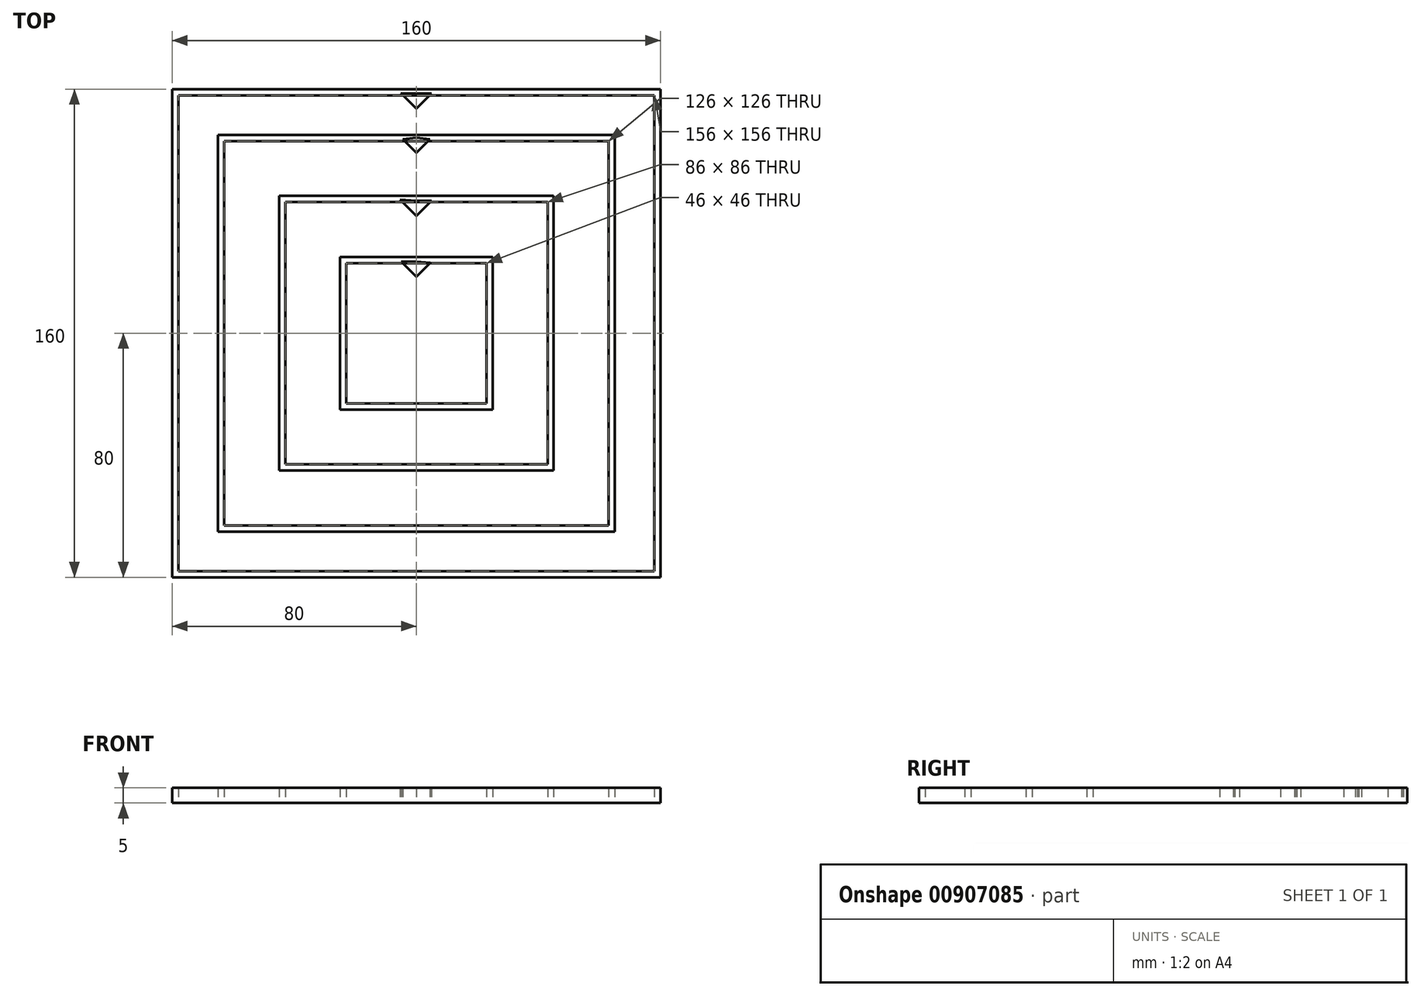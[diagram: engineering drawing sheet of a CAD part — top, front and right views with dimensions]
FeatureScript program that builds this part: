
annotation { "Feature Type Name" : "Feature", "Feature Type Description" : "" }
export const myFeature = defineFeature(function(context is Context, id is Id, definition is map)
    precondition{}
    {
        {
            var Q0;
            Q0=qCreatedBy(makeId("Top.planeOp"),FACE);
            var sketch = newSketch(context, id + "F0", { "sketchPlane" : qUnion([Q0])});
            skLineSegment(sketch, "E0.bottom", {"start": v(-80, 80) * mm, "end": v(80, 80) * mm});
            skLineSegment(sketch, "E0.top", {"start": v(-80, -80) * mm, "end": v(80, -80) * mm});
            skLineSegment(sketch, "E0.left", {"start": v(-80, 80) * mm, "end": v(-80, -80) * mm});
            skLineSegment(sketch, "E0.right", {"start": v(80, 80) * mm, "end": v(80, -80) * mm});
            skPoint(sketch, "E0.middle", {"position": v(0, 0) * mm});
            skLineSegment(sketch, "E1.bottom", {"start": v(-78, 78) * mm, "end": v(78, 78) * mm});
            skLineSegment(sketch, "E1.top", {"start": v(-78, -78) * mm, "end": v(78, -78) * mm});
            skLineSegment(sketch, "E1.left", {"start": v(-78, 78) * mm, "end": v(-78, -78) * mm});
            skLineSegment(sketch, "E1.right", {"start": v(78, 78) * mm, "end": v(78, -78) * mm});
            skLineSegment(sketch, "E2.bottom", {"start": v(-45, 45) * mm, "end": v(45, 45) * mm});
            skLineSegment(sketch, "E2.top", {"start": v(-45, -45) * mm, "end": v(45, -45) * mm});
            skLineSegment(sketch, "E2.left", {"start": v(-45, 45) * mm, "end": v(-45, -45) * mm});
            skLineSegment(sketch, "E2.right", {"start": v(45, 45) * mm, "end": v(45, -45) * mm});
            skLineSegment(sketch, "E3.bottom", {"start": v(-43, 43) * mm, "end": v(43, 43) * mm});
            skLineSegment(sketch, "E3.top", {"start": v(-43, -43) * mm, "end": v(43, -43) * mm});
            skLineSegment(sketch, "E3.left", {"start": v(-43, 43) * mm, "end": v(-43, -43) * mm});
            skLineSegment(sketch, "E3.right", {"start": v(43, 43) * mm, "end": v(43, -43) * mm});
            skLineSegment(sketch, "E4.bottom", {"start": v(-25, 25) * mm, "end": v(25, 25) * mm});
            skLineSegment(sketch, "E4.top", {"start": v(-25, -25) * mm, "end": v(25, -25) * mm});
            skLineSegment(sketch, "E4.left", {"start": v(-25, 25) * mm, "end": v(-25, -25) * mm});
            skLineSegment(sketch, "E4.right", {"start": v(25, 25) * mm, "end": v(25, -25) * mm});
            skLineSegment(sketch, "E5.bottom", {"start": v(-23, 23) * mm, "end": v(23, 23) * mm});
            skLineSegment(sketch, "E5.top", {"start": v(-23, -23) * mm, "end": v(23, -23) * mm});
            skLineSegment(sketch, "E5.left", {"start": v(-23, 23) * mm, "end": v(-23, -23) * mm});
            skLineSegment(sketch, "E5.right", {"start": v(23, 23) * mm, "end": v(23, -23) * mm});
            skLineSegment(sketch, "E6.bottom", {"start": v(-65, 65) * mm, "end": v(65, 65) * mm});
            skLineSegment(sketch, "E6.top", {"start": v(-65, -65) * mm, "end": v(65, -65) * mm});
            skLineSegment(sketch, "E6.left", {"start": v(-65, 65) * mm, "end": v(-65, -65) * mm});
            skLineSegment(sketch, "E6.right", {"start": v(65, 65) * mm, "end": v(65, -65) * mm});
            skLineSegment(sketch, "E7.bottom", {"start": v(-63, 63) * mm, "end": v(63, 63) * mm});
            skLineSegment(sketch, "E7.top", {"start": v(-63, -63) * mm, "end": v(63, -63) * mm});
            skLineSegment(sketch, "E7.left", {"start": v(-63, 63) * mm, "end": v(-63, -63) * mm});
            skLineSegment(sketch, "E7.right", {"start": v(63, 63) * mm, "end": v(63, -63) * mm});
            skSolve(sketch);
        }
        {
            var Q0;
            Q0=makeQuery(id+"F0.imprint","IMPRINT",FACE,{"disambiguationData":[TD([[makeQuery(id+"F0.imprint","IMPRINT",EDGE,{"derivedFrom":sQuery(id+"F0.wireOp",EDGE,"E0.bottom")}),-1.0]])]});
            var Q1;
            Q1=makeQuery(id+"F0.imprint","IMPRINT",FACE,{"disambiguationData":[TD([[makeQuery(id+"F0.imprint","IMPRINT",EDGE,{"derivedFrom":sQuery(id+"F0.wireOp",EDGE,"E6.bottom")}),-1.0]])]});
            var Q2;
            Q2=makeQuery(id+"F0.imprint","IMPRINT",FACE,{"disambiguationData":[TD([[makeQuery(id+"F0.imprint","IMPRINT",EDGE,{"derivedFrom":sQuery(id+"F0.wireOp",EDGE,"E2.bottom")}),-1.0]])]});
            var Q3;
            Q3=makeQuery(id+"F0.imprint","IMPRINT",FACE,{"disambiguationData":[TD([[makeQuery(id+"F0.imprint","IMPRINT",EDGE,{"derivedFrom":sQuery(id+"F0.wireOp",EDGE,"E4.bottom")}),-1.0]])]});
            extrude(context, id + "F1", {"entities" : qUnion([Q0, Q1, Q2, Q3]), "depth" : 5 * mm, "offsetDistance" : 25 * mm});
        }
        {
            var Q0;
            Q0=qCreatedBy(makeId("Top.planeOp"),FACE);
            var sketch = newSketch(context, id + "F2", { "sketchPlane" : qUnion([Q0])});
            skLineSegment(sketch, "E8", {"start": v(0, 78.6) * mm, "end": v(0, 73.6) * mm});
            skLineSegment(sketch, "E9", {"start": v(0, 73.6) * mm, "end": v(-5.12, 78.73) * mm});
            skLineSegment(sketch, "E10", {"start": v(-5.12, 78.73) * mm, "end": v(0, 78.6) * mm});
            skLineSegment(sketch, "E11", {"start": v(0, 78.6) * mm, "end": v(5, 78.6) * mm});
            skLineSegment(sketch, "E12", {"start": v(5, 78.6) * mm, "end": v(0, 73.6) * mm});
            skLineSegment(sketch, "E13", {"start": v(0, 64.13) * mm, "end": v(0, 59.13) * mm});
            skLineSegment(sketch, "E14", {"start": v(0, 59.13) * mm, "end": v(-4.45, 63.58) * mm});
            skLineSegment(sketch, "E15", {"start": v(-4.45, 63.58) * mm, "end": v(0, 64.13) * mm});
            skLineSegment(sketch, "E16", {"start": v(0, 59.13) * mm, "end": v(4.45, 63.58) * mm});
            skLineSegment(sketch, "E17", {"start": v(4.45, 63.58) * mm, "end": v(0, 64.13) * mm});
            skLineSegment(sketch, "E18", {"start": v(0, 43.45) * mm, "end": v(0, 38.45) * mm});
            skLineSegment(sketch, "E19", {"start": v(0, 38.45) * mm, "end": v(-5.32, 43.76) * mm});
            skLineSegment(sketch, "E20", {"start": v(-5.32, 43.76) * mm, "end": v(0, 43.45) * mm});
            skLineSegment(sketch, "E21", {"start": v(5, 43.45) * mm, "end": v(0, 38.45) * mm});
            skLineSegment(sketch, "E22", {"start": v(5, 43.45) * mm, "end": v(0, 43.45) * mm});
            skLineSegment(sketch, "E23", {"start": v(0, 23.5) * mm, "end": v(0, 18.5) * mm});
            skLineSegment(sketch, "E24", {"start": v(0, 18.5) * mm, "end": v(4.6, 23.1) * mm});
            skLineSegment(sketch, "E25", {"start": v(4.6, 23.1) * mm, "end": v(0, 23.5) * mm});
            skLineSegment(sketch, "E26", {"start": v(-5, 23.5) * mm, "end": v(0, 18.5) * mm});
            skLineSegment(sketch, "E27", {"start": v(-5, 23.5) * mm, "end": v(0, 23.5) * mm});
            skSolve(sketch);
        }
        {
            var Q0;
            Q0=makeQuery(id+"F2.imprint","IMPRINT",FACE,{"disambiguationData":[TD([[makeQuery(id+"F2.imprint","IMPRINT",EDGE,{"derivedFrom":sQuery(id+"F2.wireOp",EDGE,"E8")}),-1.0]])]});
            var Q1;
            Q1=makeQuery(id+"F2.imprint","IMPRINT",FACE,{"disambiguationData":[TD([[makeQuery(id+"F2.imprint","IMPRINT",EDGE,{"derivedFrom":sQuery(id+"F2.wireOp",EDGE,"E8")}),1.0]])]});
            var Q2;
            Q2=makeQuery(id+"F2.imprint","IMPRINT",FACE,{"disambiguationData":[TD([[makeQuery(id+"F2.imprint","IMPRINT",EDGE,{"derivedFrom":sQuery(id+"F2.wireOp",EDGE,"E13")}),1.0]])]});
            var Q3;
            Q3=makeQuery(id+"F2.imprint","IMPRINT",FACE,{"disambiguationData":[TD([[makeQuery(id+"F2.imprint","IMPRINT",EDGE,{"derivedFrom":sQuery(id+"F2.wireOp",EDGE,"E13")}),-1.0]])]});
            var Q4;
            Q4=makeQuery(id+"F2.imprint","IMPRINT",FACE,{"disambiguationData":[TD([[makeQuery(id+"F2.imprint","IMPRINT",EDGE,{"derivedFrom":sQuery(id+"F2.wireOp",EDGE,"E18")}),-1.0]])]});
            var Q5;
            Q5=makeQuery(id+"F2.imprint","IMPRINT",FACE,{"disambiguationData":[TD([[makeQuery(id+"F2.imprint","IMPRINT",EDGE,{"derivedFrom":sQuery(id+"F2.wireOp",EDGE,"E18")}),1.0]])]});
            var Q6;
            Q6=makeQuery(id+"F2.imprint","IMPRINT",FACE,{"disambiguationData":[TD([[makeQuery(id+"F2.imprint","IMPRINT",EDGE,{"derivedFrom":sQuery(id+"F2.wireOp",EDGE,"E23")}),-1.0]])]});
            var Q7;
            Q7=makeQuery(id+"F2.imprint","IMPRINT",FACE,{"disambiguationData":[TD([[makeQuery(id+"F2.imprint","IMPRINT",EDGE,{"derivedFrom":sQuery(id+"F2.wireOp",EDGE,"E23")}),1.0]])]});
            extrude(context, id + "F3", {"entities" : qUnion([Q0, Q1, Q2, Q3, Q4, Q5, Q6, Q7]), "depth" : 5 * mm, "offsetDistance" : 25 * mm});
        }
    });
